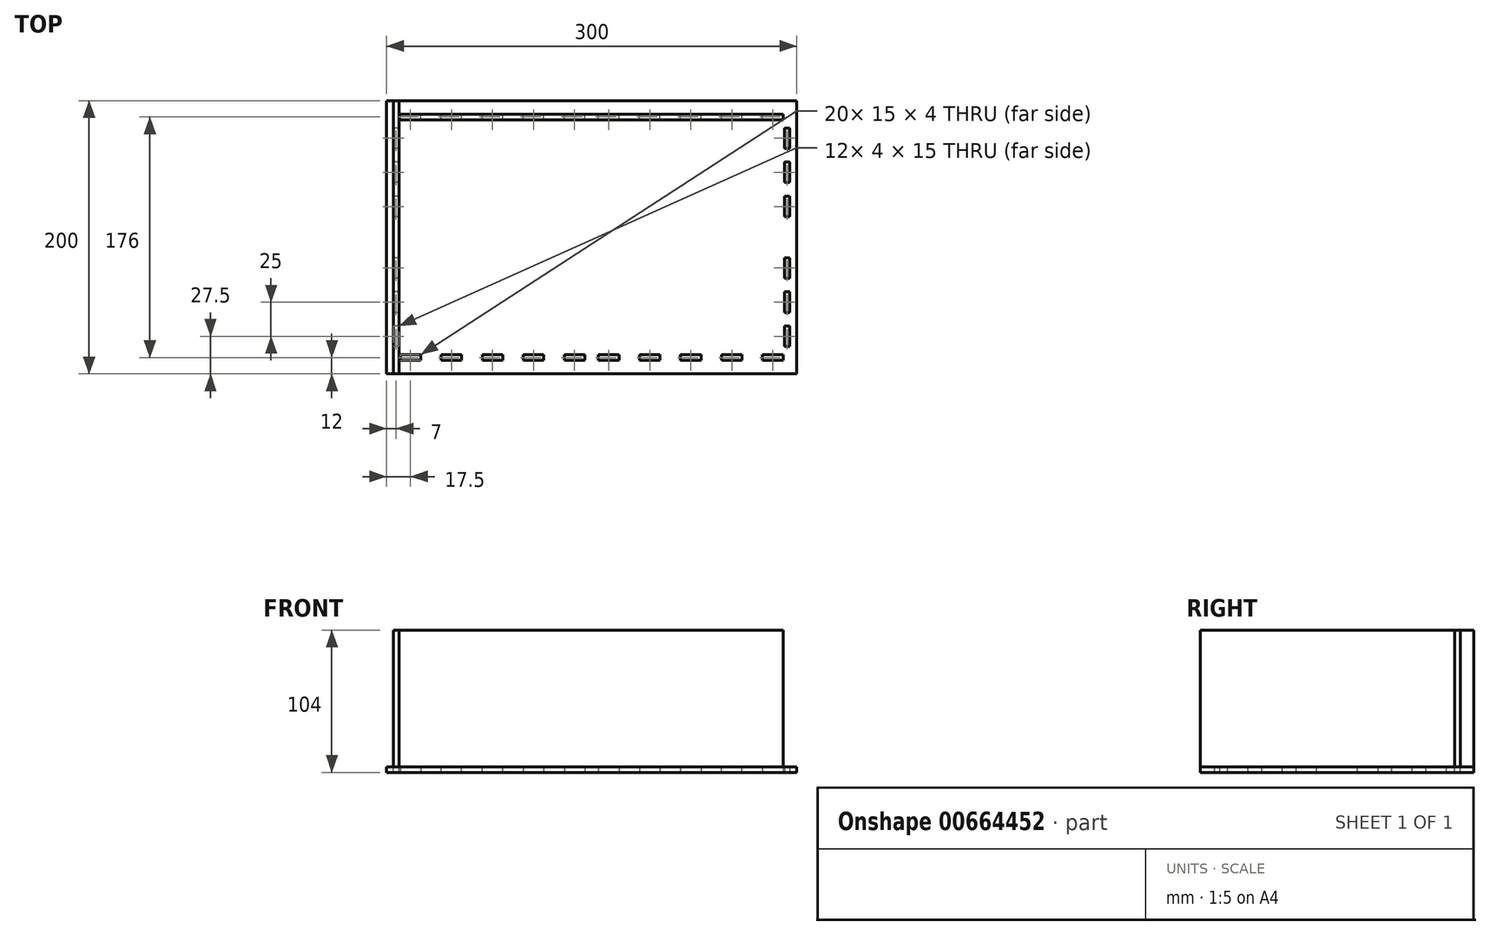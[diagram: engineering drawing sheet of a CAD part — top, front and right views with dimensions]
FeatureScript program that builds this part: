
annotation { "Feature Type Name" : "Feature", "Feature Type Description" : "" }
export const myFeature = defineFeature(function(context is Context, id is Id, definition is map)
    precondition{}
    {
        {
            assignVariable(context, id + "F0", {"name" : "material_thickness", "anyValue" : 4});
        }
        {
            var Q0;
            Q0=qCreatedBy(makeId("Top.planeOp"),FACE);
            var sketch = newSketch(context, id + "F1", { "sketchPlane" : qUnion([Q0])});
            skLineSegment(sketch, "E0.bottom", {"start": v(150, -100) * mm, "end": v(-150, -100) * mm});
            skLineSegment(sketch, "E0.top", {"start": v(150, 100) * mm, "end": v(-150, 100) * mm});
            skLineSegment(sketch, "E0.left", {"start": v(150, -100) * mm, "end": v(150, 100) * mm});
            skLineSegment(sketch, "E0.right", {"start": v(-150, -100) * mm, "end": v(-150, 100) * mm});
            skPoint(sketch, "E0.middle", {"position": v(0, 0) * mm});
            skLineSegment(sketch, "E1", {"start": v(0, 176.5) * mm, "end": v(0, -168.45) * mm, "construction": true});
            skPoint(sketch, "E1.endSnap0", {"position": v(0, -100) * mm});
            skLineSegment(sketch, "E2", {"start": v(-207.53, 0) * mm, "end": v(211.83, 0) * mm, "construction": true});
            skPoint(sketch, "E2.endSnap0", {"position": v(150, 0) * mm});
            skLineSegment(sketch, "E3.bottom", {"start": v(-125, 86) * mm, "end": v(-140, 86) * mm});
            skLineSegment(sketch, "E3.top", {"start": v(-125, 90) * mm, "end": v(-140, 90) * mm});
            skLineSegment(sketch, "E3.left", {"start": v(-125, 86) * mm, "end": v(-125, 90) * mm});
            skLineSegment(sketch, "E3.right", {"start": v(-140, 86) * mm, "end": v(-140, 90) * mm});
            skLineSegment(sketch, "E4.1.0.0", {"start": v(-95, 90) * mm, "end": v(-110, 90) * mm});
            skLineSegment(sketch, "E4.1.0.1", {"start": v(-110, 86) * mm, "end": v(-110, 90) * mm});
            skLineSegment(sketch, "E4.1.0.2", {"start": v(-95, 86) * mm, "end": v(-110, 86) * mm});
            skLineSegment(sketch, "E4.1.0.3", {"start": v(-95, 86) * mm, "end": v(-95, 90) * mm});
            skLineSegment(sketch, "E4.2.0.0", {"start": v(-65, 90) * mm, "end": v(-80, 90) * mm});
            skLineSegment(sketch, "E4.2.0.1", {"start": v(-80, 86) * mm, "end": v(-80, 90) * mm});
            skLineSegment(sketch, "E4.2.0.2", {"start": v(-65, 86) * mm, "end": v(-80, 86) * mm});
            skLineSegment(sketch, "E4.2.0.3", {"start": v(-65, 86) * mm, "end": v(-65, 90) * mm});
            skLineSegment(sketch, "E4.3.0.0", {"start": v(-35, 90) * mm, "end": v(-50, 90) * mm});
            skLineSegment(sketch, "E4.3.0.1", {"start": v(-50, 86) * mm, "end": v(-50, 90) * mm});
            skLineSegment(sketch, "E4.3.0.2", {"start": v(-35, 86) * mm, "end": v(-50, 86) * mm});
            skLineSegment(sketch, "E4.3.0.3", {"start": v(-35, 86) * mm, "end": v(-35, 90) * mm});
            skLineSegment(sketch, "E4.4.0.0", {"start": v(-5, 90) * mm, "end": v(-20, 90) * mm});
            skLineSegment(sketch, "E4.4.0.1", {"start": v(-20, 86) * mm, "end": v(-20, 90) * mm});
            skLineSegment(sketch, "E4.4.0.2", {"start": v(-5, 86) * mm, "end": v(-20, 86) * mm});
            skLineSegment(sketch, "E4.4.0.3", {"start": v(-5, 86) * mm, "end": v(-5, 90) * mm});
            skLineSegment(sketch, "E4.direction1", {"start": v(-140, 90) * mm, "end": v(-110, 90) * mm, "construction": true});
            skLineSegment(sketch, "E5.MirrorCS", {"start": v(5, 90) * mm, "end": v(20, 90) * mm});
            skLineSegment(sketch, "E6.MirrorCS", {"start": v(5, 86) * mm, "end": v(20, 86) * mm});
            skLineSegment(sketch, "E7.MirrorCS", {"start": v(5, 86) * mm, "end": v(5, 90) * mm});
            skLineSegment(sketch, "E8.MirrorCS", {"start": v(20, 86) * mm, "end": v(20, 90) * mm});
            skLineSegment(sketch, "E9.MirrorCS", {"start": v(110, 86) * mm, "end": v(110, 90) * mm});
            skLineSegment(sketch, "E10.MirrorCS", {"start": v(125, 86) * mm, "end": v(125, 90) * mm});
            skLineSegment(sketch, "E11.MirrorCS", {"start": v(50, 86) * mm, "end": v(50, 90) * mm});
            skLineSegment(sketch, "E12.MirrorCS", {"start": v(140, 86) * mm, "end": v(140, 90) * mm});
            skLineSegment(sketch, "E13.MirrorCS", {"start": v(95, 86) * mm, "end": v(95, 90) * mm});
            skLineSegment(sketch, "E14.MirrorCS", {"start": v(35, 86) * mm, "end": v(35, 90) * mm});
            skLineSegment(sketch, "E15.MirrorCS", {"start": v(80, 86) * mm, "end": v(80, 90) * mm});
            skLineSegment(sketch, "E16.MirrorCS", {"start": v(65, 86) * mm, "end": v(65, 90) * mm});
            skLineSegment(sketch, "E17.MirrorCS", {"start": v(125, 90) * mm, "end": v(140, 90) * mm});
            skLineSegment(sketch, "E18.MirrorCS", {"start": v(35, 86) * mm, "end": v(50, 86) * mm});
            skLineSegment(sketch, "E19.MirrorCS", {"start": v(95, 90) * mm, "end": v(110, 90) * mm});
            skLineSegment(sketch, "E20.MirrorCS", {"start": v(65, 86) * mm, "end": v(80, 86) * mm});
            skLineSegment(sketch, "E21.MirrorCS", {"start": v(95, 86) * mm, "end": v(110, 86) * mm});
            skLineSegment(sketch, "E22.MirrorCS", {"start": v(140, 90) * mm, "end": v(110, 90) * mm, "construction": true});
            skLineSegment(sketch, "E23.MirrorCS", {"start": v(65, 90) * mm, "end": v(80, 90) * mm});
            skLineSegment(sketch, "E24.MirrorCS", {"start": v(125, 86) * mm, "end": v(140, 86) * mm});
            skLineSegment(sketch, "E25.MirrorCS", {"start": v(35, 90) * mm, "end": v(50, 90) * mm});
            skLineSegment(sketch, "E26.bottom", {"start": v(141, 80) * mm, "end": v(145, 80) * mm});
            skLineSegment(sketch, "E26.top", {"start": v(141, 65) * mm, "end": v(145, 65) * mm});
            skLineSegment(sketch, "E26.left", {"start": v(141, 80) * mm, "end": v(141, 65) * mm});
            skLineSegment(sketch, "E26.right", {"start": v(145, 80) * mm, "end": v(145, 65) * mm});
            skLineSegment(sketch, "E27.0.1.0", {"start": v(145, 55) * mm, "end": v(145, 40) * mm});
            skLineSegment(sketch, "E27.0.1.1", {"start": v(141, 55) * mm, "end": v(145, 55) * mm});
            skLineSegment(sketch, "E27.0.1.2", {"start": v(141, 55) * mm, "end": v(141, 40) * mm});
            skLineSegment(sketch, "E27.0.1.3", {"start": v(141, 40) * mm, "end": v(145, 40) * mm});
            skLineSegment(sketch, "E27.0.2.0", {"start": v(145, 30) * mm, "end": v(145, 15) * mm});
            skLineSegment(sketch, "E27.0.2.1", {"start": v(141, 30) * mm, "end": v(145, 30) * mm});
            skLineSegment(sketch, "E27.0.2.2", {"start": v(141, 30) * mm, "end": v(141, 15) * mm});
            skLineSegment(sketch, "E27.0.2.3", {"start": v(141, 15) * mm, "end": v(145, 15) * mm});
            skLineSegment(sketch, "E27.direction1", {"start": v(145, 65) * mm, "end": v(170, 65) * mm, "construction": true});
            skLineSegment(sketch, "E27.direction2", {"start": v(145, 65) * mm, "end": v(145, 40) * mm, "construction": true});
            skLineSegment(sketch, "E28.MirrorCS", {"start": v(141, -55) * mm, "end": v(141, -40) * mm});
            skLineSegment(sketch, "E29.MirrorCS", {"start": v(141, -40) * mm, "end": v(145, -40) * mm});
            skLineSegment(sketch, "E30.MirrorCS", {"start": v(141, -30) * mm, "end": v(145, -30) * mm});
            skLineSegment(sketch, "E31.MirrorCS", {"start": v(145, -30) * mm, "end": v(145, -15) * mm});
            skLineSegment(sketch, "E32.MirrorCS", {"start": v(141, -30) * mm, "end": v(141, -15) * mm});
            skLineSegment(sketch, "E33.MirrorCS", {"start": v(141, -15) * mm, "end": v(145, -15) * mm});
            skLineSegment(sketch, "E34.MirrorCS", {"start": v(141, -55) * mm, "end": v(145, -55) * mm});
            skLineSegment(sketch, "E35.MirrorCS", {"start": v(141, -65) * mm, "end": v(145, -65) * mm});
            skLineSegment(sketch, "E36.MirrorCS", {"start": v(145, -80) * mm, "end": v(145, -65) * mm});
            skLineSegment(sketch, "E37.MirrorCS", {"start": v(141, -80) * mm, "end": v(141, -65) * mm});
            skLineSegment(sketch, "E38.MirrorCS", {"start": v(141, -80) * mm, "end": v(145, -80) * mm});
            skLineSegment(sketch, "E39.MirrorCS", {"start": v(145, -55) * mm, "end": v(145, -40) * mm});
            skLineSegment(sketch, "E40.MirrorCS", {"start": v(140, -86) * mm, "end": v(140, -90) * mm});
            skLineSegment(sketch, "E41.MirrorCS", {"start": v(125, -86) * mm, "end": v(140, -86) * mm});
            skLineSegment(sketch, "E42.MirrorCS", {"start": v(125, -86) * mm, "end": v(125, -90) * mm});
            skLineSegment(sketch, "E43.MirrorCS", {"start": v(125, -90) * mm, "end": v(140, -90) * mm});
            skLineSegment(sketch, "E44.MirrorCS", {"start": v(110, -86) * mm, "end": v(110, -90) * mm});
            skLineSegment(sketch, "E45.MirrorCS", {"start": v(95, -90) * mm, "end": v(110, -90) * mm});
            skLineSegment(sketch, "E46.MirrorCS", {"start": v(95, -86) * mm, "end": v(95, -90) * mm});
            skLineSegment(sketch, "E47.MirrorCS", {"start": v(95, -86) * mm, "end": v(110, -86) * mm});
            skLineSegment(sketch, "E48.MirrorCS", {"start": v(80, -86) * mm, "end": v(80, -90) * mm});
            skLineSegment(sketch, "E49.MirrorCS", {"start": v(65, -90) * mm, "end": v(80, -90) * mm});
            skLineSegment(sketch, "E50.MirrorCS", {"start": v(65, -86) * mm, "end": v(65, -90) * mm});
            skLineSegment(sketch, "E51.MirrorCS", {"start": v(65, -86) * mm, "end": v(80, -86) * mm});
            skLineSegment(sketch, "E52.MirrorCS", {"start": v(50, -86) * mm, "end": v(50, -90) * mm});
            skLineSegment(sketch, "E53.MirrorCS", {"start": v(35, -90) * mm, "end": v(50, -90) * mm});
            skLineSegment(sketch, "E54.MirrorCS", {"start": v(35, -86) * mm, "end": v(50, -86) * mm});
            skLineSegment(sketch, "E55.MirrorCS", {"start": v(35, -86) * mm, "end": v(35, -90) * mm});
            skLineSegment(sketch, "E56.MirrorCS", {"start": v(20, -86) * mm, "end": v(20, -90) * mm});
            skLineSegment(sketch, "E57.MirrorCS", {"start": v(5, -90) * mm, "end": v(20, -90) * mm});
            skLineSegment(sketch, "E58.MirrorCS", {"start": v(5, -86) * mm, "end": v(20, -86) * mm});
            skLineSegment(sketch, "E59.MirrorCS", {"start": v(5, -86) * mm, "end": v(5, -90) * mm});
            skLineSegment(sketch, "E60.MirrorCS", {"start": v(-5, -86) * mm, "end": v(-5, -90) * mm});
            skLineSegment(sketch, "E61.MirrorCS", {"start": v(-5, -90) * mm, "end": v(-20, -90) * mm});
            skLineSegment(sketch, "E62.MirrorCS", {"start": v(-5, -86) * mm, "end": v(-20, -86) * mm});
            skLineSegment(sketch, "E63.MirrorCS", {"start": v(-20, -86) * mm, "end": v(-20, -90) * mm});
            skLineSegment(sketch, "E64.MirrorCS", {"start": v(-35, -86) * mm, "end": v(-35, -90) * mm});
            skLineSegment(sketch, "E65.MirrorCS", {"start": v(-35, -90) * mm, "end": v(-50, -90) * mm});
            skLineSegment(sketch, "E66.MirrorCS", {"start": v(-35, -86) * mm, "end": v(-50, -86) * mm});
            skLineSegment(sketch, "E67.MirrorCS", {"start": v(-50, -86) * mm, "end": v(-50, -90) * mm});
            skLineSegment(sketch, "E68.MirrorCS", {"start": v(-65, -86) * mm, "end": v(-65, -90) * mm});
            skLineSegment(sketch, "E69.MirrorCS", {"start": v(-65, -90) * mm, "end": v(-80, -90) * mm});
            skLineSegment(sketch, "E70.MirrorCS", {"start": v(-65, -86) * mm, "end": v(-80, -86) * mm});
            skLineSegment(sketch, "E71.MirrorCS", {"start": v(-80, -86) * mm, "end": v(-80, -90) * mm});
            skLineSegment(sketch, "E72.MirrorCS", {"start": v(-95, -86) * mm, "end": v(-95, -90) * mm});
            skLineSegment(sketch, "E73.MirrorCS", {"start": v(-95, -90) * mm, "end": v(-110, -90) * mm});
            skLineSegment(sketch, "E74.MirrorCS", {"start": v(-95, -86) * mm, "end": v(-110, -86) * mm});
            skLineSegment(sketch, "E75.MirrorCS", {"start": v(-110, -86) * mm, "end": v(-110, -90) * mm});
            skLineSegment(sketch, "E76.MirrorCS", {"start": v(-125, -86) * mm, "end": v(-125, -90) * mm});
            skLineSegment(sketch, "E77.MirrorCS", {"start": v(-125, -86) * mm, "end": v(-140, -86) * mm});
            skLineSegment(sketch, "E78.MirrorCS", {"start": v(-140, -86) * mm, "end": v(-140, -90) * mm});
            skLineSegment(sketch, "E79.MirrorCS", {"start": v(-125, -90) * mm, "end": v(-140, -90) * mm});
            skLineSegment(sketch, "E80.MirrorCS", {"start": v(-141, 80) * mm, "end": v(-145, 80) * mm});
            skLineSegment(sketch, "E81.MirrorCS", {"start": v(-141, 80) * mm, "end": v(-141, 65) * mm});
            skLineSegment(sketch, "E82.MirrorCS", {"start": v(-145, 80) * mm, "end": v(-145, 65) * mm});
            skLineSegment(sketch, "E83.MirrorCS", {"start": v(-141, 65) * mm, "end": v(-145, 65) * mm});
            skLineSegment(sketch, "E84.MirrorCS", {"start": v(-141, 55) * mm, "end": v(-141, 40) * mm});
            skLineSegment(sketch, "E85.MirrorCS", {"start": v(-141, 40) * mm, "end": v(-145, 40) * mm});
            skLineSegment(sketch, "E86.MirrorCS", {"start": v(-141, 55) * mm, "end": v(-145, 55) * mm});
            skLineSegment(sketch, "E87.MirrorCS", {"start": v(-145, 55) * mm, "end": v(-145, 40) * mm});
            skLineSegment(sketch, "E88.MirrorCS", {"start": v(-141, 30) * mm, "end": v(-145, 30) * mm});
            skLineSegment(sketch, "E89.MirrorCS", {"start": v(-141, 30) * mm, "end": v(-141, 15) * mm});
            skLineSegment(sketch, "E90.MirrorCS", {"start": v(-145, 30) * mm, "end": v(-145, 15) * mm});
            skLineSegment(sketch, "E91.MirrorCS", {"start": v(-141, 15) * mm, "end": v(-145, 15) * mm});
            skLineSegment(sketch, "E92.MirrorCS", {"start": v(-141, -30) * mm, "end": v(-141, -15) * mm});
            skLineSegment(sketch, "E93.MirrorCS", {"start": v(-145, -30) * mm, "end": v(-145, -15) * mm});
            skLineSegment(sketch, "E94.MirrorCS", {"start": v(-141, -30) * mm, "end": v(-145, -30) * mm});
            skLineSegment(sketch, "E95.MirrorCS", {"start": v(-141, -15) * mm, "end": v(-145, -15) * mm});
            skLineSegment(sketch, "E96.MirrorCS", {"start": v(-145, -55) * mm, "end": v(-145, -40) * mm});
            skLineSegment(sketch, "E97.MirrorCS", {"start": v(-141, -55) * mm, "end": v(-141, -40) * mm});
            skLineSegment(sketch, "E98.MirrorCS", {"start": v(-141, -55) * mm, "end": v(-145, -55) * mm});
            skLineSegment(sketch, "E99.MirrorCS", {"start": v(-141, -40) * mm, "end": v(-145, -40) * mm});
            skLineSegment(sketch, "E100.MirrorCS", {"start": v(-141, -65) * mm, "end": v(-145, -65) * mm});
            skLineSegment(sketch, "E101.MirrorCS", {"start": v(-141, -80) * mm, "end": v(-141, -65) * mm});
            skLineSegment(sketch, "E102.MirrorCS", {"start": v(-145, -80) * mm, "end": v(-145, -65) * mm});
            skLineSegment(sketch, "E103.MirrorCS", {"start": v(-141, -80) * mm, "end": v(-145, -80) * mm});
            skSolve(sketch);
        }
        {
            var Q0;
            Q0=makeQuery(id+"F1.imprint","IMPRINT",FACE,{"disambiguationData":[TD([[makeQuery(id+"F1.imprint","IMPRINT",EDGE,{"derivedFrom":sQuery(id+"F1.wireOp",EDGE,"E0.bottom")}),-1.0]])]});
            extrude(context, id + "F2", {"entities" : qUnion([Q0]), "depth" : (getVariable(context, 'material_thickness')) * mm});
        }
        {
            var Q0;
            Q0=makeQuery(id+"F2.opExtrude","CAP_FACE",FACE,{"disambiguationData":[OSD([sQuery(id+"F1.wireOp",EDGE,"E0.bottom"),sQuery(id+"F1.wireOp",EDGE,"E0.top"),sQuery(id+"F1.wireOp",EDGE,"E0.left"),sQuery(id+"F1.wireOp",EDGE,"E0.right"),sQuery(id+"F1.wireOp",EDGE,"E3.bottom"),sQuery(id+"F1.wireOp",EDGE,"E3.top"),sQuery(id+"F1.wireOp",EDGE,"E3.left"),sQuery(id+"F1.wireOp",EDGE,"E3.right"),sQuery(id+"F1.wireOp",EDGE,"E4.1.0.0"),sQuery(id+"F1.wireOp",EDGE,"E4.1.0.1"),sQuery(id+"F1.wireOp",EDGE,"E4.1.0.2"),sQuery(id+"F1.wireOp",EDGE,"E4.1.0.3"),sQuery(id+"F1.wireOp",EDGE,"E4.2.0.0"),sQuery(id+"F1.wireOp",EDGE,"E4.2.0.1"),sQuery(id+"F1.wireOp",EDGE,"E4.2.0.2"),sQuery(id+"F1.wireOp",EDGE,"E4.2.0.3"),sQuery(id+"F1.wireOp",EDGE,"E4.3.0.0"),sQuery(id+"F1.wireOp",EDGE,"E4.3.0.1"),sQuery(id+"F1.wireOp",EDGE,"E4.3.0.2"),sQuery(id+"F1.wireOp",EDGE,"E4.3.0.3"),sQuery(id+"F1.wireOp",EDGE,"E4.4.0.0"),sQuery(id+"F1.wireOp",EDGE,"E4.4.0.1"),sQuery(id+"F1.wireOp",EDGE,"E4.4.0.2"),sQuery(id+"F1.wireOp",EDGE,"E4.4.0.3"),sQuery(id+"F1.wireOp",EDGE,"E5.MirrorCS"),sQuery(id+"F1.wireOp",EDGE,"E6.MirrorCS"),sQuery(id+"F1.wireOp",EDGE,"E7.MirrorCS"),sQuery(id+"F1.wireOp",EDGE,"E8.MirrorCS"),sQuery(id+"F1.wireOp",EDGE,"E9.MirrorCS"),sQuery(id+"F1.wireOp",EDGE,"E10.MirrorCS"),sQuery(id+"F1.wireOp",EDGE,"E11.MirrorCS"),sQuery(id+"F1.wireOp",EDGE,"E12.MirrorCS"),sQuery(id+"F1.wireOp",EDGE,"E13.MirrorCS"),sQuery(id+"F1.wireOp",EDGE,"E14.MirrorCS"),sQuery(id+"F1.wireOp",EDGE,"E15.MirrorCS"),sQuery(id+"F1.wireOp",EDGE,"E16.MirrorCS"),sQuery(id+"F1.wireOp",EDGE,"E17.MirrorCS"),sQuery(id+"F1.wireOp",EDGE,"E18.MirrorCS"),sQuery(id+"F1.wireOp",EDGE,"E19.MirrorCS"),sQuery(id+"F1.wireOp",EDGE,"E20.MirrorCS"),sQuery(id+"F1.wireOp",EDGE,"E21.MirrorCS"),sQuery(id+"F1.wireOp",EDGE,"E23.MirrorCS"),sQuery(id+"F1.wireOp",EDGE,"E24.MirrorCS"),sQuery(id+"F1.wireOp",EDGE,"E25.MirrorCS"),sQuery(id+"F1.wireOp",EDGE,"E26.bottom"),sQuery(id+"F1.wireOp",EDGE,"E26.top"),sQuery(id+"F1.wireOp",EDGE,"E26.left"),sQuery(id+"F1.wireOp",EDGE,"E26.right"),sQuery(id+"F1.wireOp",EDGE,"E27.0.1.0"),sQuery(id+"F1.wireOp",EDGE,"E27.0.1.1"),sQuery(id+"F1.wireOp",EDGE,"E27.0.1.2"),sQuery(id+"F1.wireOp",EDGE,"E27.0.1.3"),sQuery(id+"F1.wireOp",EDGE,"E27.0.2.0"),sQuery(id+"F1.wireOp",EDGE,"E27.0.2.1"),sQuery(id+"F1.wireOp",EDGE,"E27.0.2.2"),sQuery(id+"F1.wireOp",EDGE,"E27.0.2.3"),sQuery(id+"F1.wireOp",EDGE,"E28.MirrorCS"),sQuery(id+"F1.wireOp",EDGE,"E30.MirrorCS"),sQuery(id+"F1.wireOp",EDGE,"E31.MirrorCS"),sQuery(id+"F1.wireOp",EDGE,"E32.MirrorCS"),sQuery(id+"F1.wireOp",EDGE,"E33.MirrorCS"),sQuery(id+"F1.wireOp",EDGE,"E29.MirrorCS"),sQuery(id+"F1.wireOp",EDGE,"E34.MirrorCS"),sQuery(id+"F1.wireOp",EDGE,"E35.MirrorCS"),sQuery(id+"F1.wireOp",EDGE,"E36.MirrorCS"),sQuery(id+"F1.wireOp",EDGE,"E37.MirrorCS"),sQuery(id+"F1.wireOp",EDGE,"E38.MirrorCS"),sQuery(id+"F1.wireOp",EDGE,"E39.MirrorCS"),sQuery(id+"F1.wireOp",EDGE,"E40.MirrorCS"),sQuery(id+"F1.wireOp",EDGE,"E41.MirrorCS"),sQuery(id+"F1.wireOp",EDGE,"E42.MirrorCS"),sQuery(id+"F1.wireOp",EDGE,"E43.MirrorCS"),sQuery(id+"F1.wireOp",EDGE,"E44.MirrorCS"),sQuery(id+"F1.wireOp",EDGE,"E45.MirrorCS"),sQuery(id+"F1.wireOp",EDGE,"E46.MirrorCS"),sQuery(id+"F1.wireOp",EDGE,"E47.MirrorCS"),sQuery(id+"F1.wireOp",EDGE,"E48.MirrorCS"),sQuery(id+"F1.wireOp",EDGE,"E49.MirrorCS"),sQuery(id+"F1.wireOp",EDGE,"E50.MirrorCS"),sQuery(id+"F1.wireOp",EDGE,"E51.MirrorCS"),sQuery(id+"F1.wireOp",EDGE,"E52.MirrorCS"),sQuery(id+"F1.wireOp",EDGE,"E53.MirrorCS"),sQuery(id+"F1.wireOp",EDGE,"E54.MirrorCS"),sQuery(id+"F1.wireOp",EDGE,"E55.MirrorCS"),sQuery(id+"F1.wireOp",EDGE,"E56.MirrorCS"),sQuery(id+"F1.wireOp",EDGE,"E57.MirrorCS"),sQuery(id+"F1.wireOp",EDGE,"E58.MirrorCS"),sQuery(id+"F1.wireOp",EDGE,"E59.MirrorCS"),sQuery(id+"F1.wireOp",EDGE,"E60.MirrorCS"),sQuery(id+"F1.wireOp",EDGE,"E61.MirrorCS"),sQuery(id+"F1.wireOp",EDGE,"E62.MirrorCS"),sQuery(id+"F1.wireOp",EDGE,"E63.MirrorCS"),sQuery(id+"F1.wireOp",EDGE,"E64.MirrorCS"),sQuery(id+"F1.wireOp",EDGE,"E65.MirrorCS"),sQuery(id+"F1.wireOp",EDGE,"E66.MirrorCS"),sQuery(id+"F1.wireOp",EDGE,"E67.MirrorCS"),sQuery(id+"F1.wireOp",EDGE,"E68.MirrorCS"),sQuery(id+"F1.wireOp",EDGE,"E69.MirrorCS"),sQuery(id+"F1.wireOp",EDGE,"E70.MirrorCS"),sQuery(id+"F1.wireOp",EDGE,"E71.MirrorCS"),sQuery(id+"F1.wireOp",EDGE,"E72.MirrorCS"),sQuery(id+"F1.wireOp",EDGE,"E73.MirrorCS"),sQuery(id+"F1.wireOp",EDGE,"E74.MirrorCS"),sQuery(id+"F1.wireOp",EDGE,"E75.MirrorCS"),sQuery(id+"F1.wireOp",EDGE,"E76.MirrorCS"),sQuery(id+"F1.wireOp",EDGE,"E77.MirrorCS"),sQuery(id+"F1.wireOp",EDGE,"E78.MirrorCS"),sQuery(id+"F1.wireOp",EDGE,"E79.MirrorCS"),sQuery(id+"F1.wireOp",EDGE,"E80.MirrorCS"),sQuery(id+"F1.wireOp",EDGE,"E81.MirrorCS"),sQuery(id+"F1.wireOp",EDGE,"E82.MirrorCS"),sQuery(id+"F1.wireOp",EDGE,"E83.MirrorCS"),sQuery(id+"F1.wireOp",EDGE,"E84.MirrorCS"),sQuery(id+"F1.wireOp",EDGE,"E85.MirrorCS"),sQuery(id+"F1.wireOp",EDGE,"E86.MirrorCS"),sQuery(id+"F1.wireOp",EDGE,"E87.MirrorCS"),sQuery(id+"F1.wireOp",EDGE,"E88.MirrorCS"),sQuery(id+"F1.wireOp",EDGE,"E89.MirrorCS"),sQuery(id+"F1.wireOp",EDGE,"E90.MirrorCS"),sQuery(id+"F1.wireOp",EDGE,"E91.MirrorCS"),sQuery(id+"F1.wireOp",EDGE,"E92.MirrorCS"),sQuery(id+"F1.wireOp",EDGE,"E93.MirrorCS"),sQuery(id+"F1.wireOp",EDGE,"E94.MirrorCS"),sQuery(id+"F1.wireOp",EDGE,"E95.MirrorCS"),sQuery(id+"F1.wireOp",EDGE,"E96.MirrorCS"),sQuery(id+"F1.wireOp",EDGE,"E97.MirrorCS"),sQuery(id+"F1.wireOp",EDGE,"E98.MirrorCS"),sQuery(id+"F1.wireOp",EDGE,"E99.MirrorCS"),sQuery(id+"F1.wireOp",EDGE,"E100.MirrorCS"),sQuery(id+"F1.wireOp",EDGE,"E101.MirrorCS"),sQuery(id+"F1.wireOp",EDGE,"E102.MirrorCS"),sQuery(id+"F1.wireOp",EDGE,"E103.MirrorCS")])],"isStart":false});
            var sketch = newSketch(context, id + "F3", { "sketchPlane" : qUnion([Q0])});
            skLineSegment(sketch, "E104.bottom", {"start": v(-145, -80) * mm, "end": v(-141, -80) * mm});
            skLineSegment(sketch, "E104.top", {"start": v(-145, -65) * mm, "end": v(-141, -65) * mm});
            skLineSegment(sketch, "E104.left", {"start": v(-145, -80) * mm, "end": v(-145, -65) * mm});
            skLineSegment(sketch, "E104.right", {"start": v(-141, -80) * mm, "end": v(-141, -65) * mm});
            skLineSegment(sketch, "E105.bottom", {"start": v(-145, -55) * mm, "end": v(-141, -55) * mm});
            skLineSegment(sketch, "E105.top", {"start": v(-145, -40) * mm, "end": v(-141, -40) * mm});
            skLineSegment(sketch, "E105.left", {"start": v(-145, -55) * mm, "end": v(-145, -40) * mm});
            skLineSegment(sketch, "E105.right", {"start": v(-141, -55) * mm, "end": v(-141, -40) * mm});
            skLineSegment(sketch, "E106.bottom", {"start": v(-145, -30) * mm, "end": v(-141, -30) * mm});
            skLineSegment(sketch, "E106.top", {"start": v(-145, -15) * mm, "end": v(-141, -15) * mm});
            skLineSegment(sketch, "E106.left", {"start": v(-145, -30) * mm, "end": v(-145, -15) * mm});
            skLineSegment(sketch, "E106.right", {"start": v(-141, -30) * mm, "end": v(-141, -15) * mm});
            skLineSegment(sketch, "E107.bottom", {"start": v(-145, 15) * mm, "end": v(-141, 15) * mm});
            skLineSegment(sketch, "E107.top", {"start": v(-145, 30) * mm, "end": v(-141, 30) * mm});
            skLineSegment(sketch, "E107.left", {"start": v(-145, 15) * mm, "end": v(-145, 30) * mm});
            skLineSegment(sketch, "E107.right", {"start": v(-141, 15) * mm, "end": v(-141, 30) * mm});
            skLineSegment(sketch, "E108.bottom", {"start": v(-145, 40) * mm, "end": v(-141, 40) * mm});
            skLineSegment(sketch, "E108.top", {"start": v(-145, 55) * mm, "end": v(-141, 55) * mm});
            skLineSegment(sketch, "E108.left", {"start": v(-145, 40) * mm, "end": v(-145, 55) * mm});
            skLineSegment(sketch, "E108.right", {"start": v(-141, 40) * mm, "end": v(-141, 55) * mm});
            skLineSegment(sketch, "E109.bottom", {"start": v(-145, 65) * mm, "end": v(-141, 65) * mm});
            skLineSegment(sketch, "E109.top", {"start": v(-145, 80) * mm, "end": v(-141, 80) * mm});
            skLineSegment(sketch, "E109.left", {"start": v(-145, 65) * mm, "end": v(-145, 80) * mm});
            skLineSegment(sketch, "E109.right", {"start": v(-141, 65) * mm, "end": v(-141, 80) * mm});
            skSolve(sketch);
        }
        {
            var Q0;
            Q0=makeQuery(id+"F3.imprint","IMPRINT",FACE,{"disambiguationData":[TD([[makeQuery(id+"F3.imprint","IMPRINT",EDGE,{"derivedFrom":sQuery(id+"F3.wireOp",EDGE,"E104.bottom")}),-1.0]])]});
            var Q1;
            Q1=makeQuery(id+"F3.imprint","IMPRINT",FACE,{"disambiguationData":[TD([[makeQuery(id+"F3.imprint","IMPRINT",EDGE,{"derivedFrom":sQuery(id+"F3.wireOp",EDGE,"E105.bottom")}),-1.0]])]});
            var Q2;
            Q2=makeQuery(id+"F3.imprint","IMPRINT",FACE,{"disambiguationData":[TD([[makeQuery(id+"F3.imprint","IMPRINT",EDGE,{"derivedFrom":sQuery(id+"F3.wireOp",EDGE,"E106.bottom")}),-1.0]])]});
            var Q3;
            Q3=makeQuery(id+"F3.imprint","IMPRINT",FACE,{"disambiguationData":[TD([[makeQuery(id+"F3.imprint","IMPRINT",EDGE,{"derivedFrom":sQuery(id+"F3.wireOp",EDGE,"E107.bottom")}),-1.0]])]});
            var Q4;
            Q4=makeQuery(id+"F3.imprint","IMPRINT",FACE,{"disambiguationData":[TD([[makeQuery(id+"F3.imprint","IMPRINT",EDGE,{"derivedFrom":sQuery(id+"F3.wireOp",EDGE,"E108.bottom")}),-1.0]])]});
            var Q5;
            Q5=makeQuery(id+"F3.imprint","IMPRINT",FACE,{"disambiguationData":[TD([[makeQuery(id+"F3.imprint","IMPRINT",EDGE,{"derivedFrom":sQuery(id+"F3.wireOp",EDGE,"E109.bottom")}),-1.0]])]});
            extrude(context, id + "F4", {"entities" : qUnion([Q0, Q1, Q2, Q3, Q4, Q5]), "oppositeDirection" : true, "depth" : 4 * mm});
        }
        {
            var Q0;
            Q0=makeQuery(id+"F2.opExtrude","CAP_FACE",FACE,{"disambiguationData":[OSD([sQuery(id+"F1.wireOp",EDGE,"E0.bottom"),sQuery(id+"F1.wireOp",EDGE,"E0.top"),sQuery(id+"F1.wireOp",EDGE,"E0.left"),sQuery(id+"F1.wireOp",EDGE,"E0.right"),sQuery(id+"F1.wireOp",EDGE,"E3.bottom"),sQuery(id+"F1.wireOp",EDGE,"E3.top"),sQuery(id+"F1.wireOp",EDGE,"E3.left"),sQuery(id+"F1.wireOp",EDGE,"E3.right"),sQuery(id+"F1.wireOp",EDGE,"E4.1.0.0"),sQuery(id+"F1.wireOp",EDGE,"E4.1.0.1"),sQuery(id+"F1.wireOp",EDGE,"E4.1.0.2"),sQuery(id+"F1.wireOp",EDGE,"E4.1.0.3"),sQuery(id+"F1.wireOp",EDGE,"E4.2.0.0"),sQuery(id+"F1.wireOp",EDGE,"E4.2.0.1"),sQuery(id+"F1.wireOp",EDGE,"E4.2.0.2"),sQuery(id+"F1.wireOp",EDGE,"E4.2.0.3"),sQuery(id+"F1.wireOp",EDGE,"E4.3.0.0"),sQuery(id+"F1.wireOp",EDGE,"E4.3.0.1"),sQuery(id+"F1.wireOp",EDGE,"E4.3.0.2"),sQuery(id+"F1.wireOp",EDGE,"E4.3.0.3"),sQuery(id+"F1.wireOp",EDGE,"E4.4.0.0"),sQuery(id+"F1.wireOp",EDGE,"E4.4.0.1"),sQuery(id+"F1.wireOp",EDGE,"E4.4.0.2"),sQuery(id+"F1.wireOp",EDGE,"E4.4.0.3"),sQuery(id+"F1.wireOp",EDGE,"E5.MirrorCS"),sQuery(id+"F1.wireOp",EDGE,"E6.MirrorCS"),sQuery(id+"F1.wireOp",EDGE,"E7.MirrorCS"),sQuery(id+"F1.wireOp",EDGE,"E8.MirrorCS"),sQuery(id+"F1.wireOp",EDGE,"E9.MirrorCS"),sQuery(id+"F1.wireOp",EDGE,"E10.MirrorCS"),sQuery(id+"F1.wireOp",EDGE,"E11.MirrorCS"),sQuery(id+"F1.wireOp",EDGE,"E12.MirrorCS"),sQuery(id+"F1.wireOp",EDGE,"E13.MirrorCS"),sQuery(id+"F1.wireOp",EDGE,"E14.MirrorCS"),sQuery(id+"F1.wireOp",EDGE,"E15.MirrorCS"),sQuery(id+"F1.wireOp",EDGE,"E16.MirrorCS"),sQuery(id+"F1.wireOp",EDGE,"E17.MirrorCS"),sQuery(id+"F1.wireOp",EDGE,"E18.MirrorCS"),sQuery(id+"F1.wireOp",EDGE,"E19.MirrorCS"),sQuery(id+"F1.wireOp",EDGE,"E20.MirrorCS"),sQuery(id+"F1.wireOp",EDGE,"E21.MirrorCS"),sQuery(id+"F1.wireOp",EDGE,"E23.MirrorCS"),sQuery(id+"F1.wireOp",EDGE,"E24.MirrorCS"),sQuery(id+"F1.wireOp",EDGE,"E25.MirrorCS"),sQuery(id+"F1.wireOp",EDGE,"E26.bottom"),sQuery(id+"F1.wireOp",EDGE,"E26.top"),sQuery(id+"F1.wireOp",EDGE,"E26.left"),sQuery(id+"F1.wireOp",EDGE,"E26.right"),sQuery(id+"F1.wireOp",EDGE,"E27.0.1.0"),sQuery(id+"F1.wireOp",EDGE,"E27.0.1.1"),sQuery(id+"F1.wireOp",EDGE,"E27.0.1.2"),sQuery(id+"F1.wireOp",EDGE,"E27.0.1.3"),sQuery(id+"F1.wireOp",EDGE,"E27.0.2.0"),sQuery(id+"F1.wireOp",EDGE,"E27.0.2.1"),sQuery(id+"F1.wireOp",EDGE,"E27.0.2.2"),sQuery(id+"F1.wireOp",EDGE,"E27.0.2.3"),sQuery(id+"F1.wireOp",EDGE,"E28.MirrorCS"),sQuery(id+"F1.wireOp",EDGE,"E30.MirrorCS"),sQuery(id+"F1.wireOp",EDGE,"E31.MirrorCS"),sQuery(id+"F1.wireOp",EDGE,"E32.MirrorCS"),sQuery(id+"F1.wireOp",EDGE,"E33.MirrorCS"),sQuery(id+"F1.wireOp",EDGE,"E29.MirrorCS"),sQuery(id+"F1.wireOp",EDGE,"E34.MirrorCS"),sQuery(id+"F1.wireOp",EDGE,"E35.MirrorCS"),sQuery(id+"F1.wireOp",EDGE,"E36.MirrorCS"),sQuery(id+"F1.wireOp",EDGE,"E37.MirrorCS"),sQuery(id+"F1.wireOp",EDGE,"E38.MirrorCS"),sQuery(id+"F1.wireOp",EDGE,"E39.MirrorCS"),sQuery(id+"F1.wireOp",EDGE,"E40.MirrorCS"),sQuery(id+"F1.wireOp",EDGE,"E41.MirrorCS"),sQuery(id+"F1.wireOp",EDGE,"E42.MirrorCS"),sQuery(id+"F1.wireOp",EDGE,"E43.MirrorCS"),sQuery(id+"F1.wireOp",EDGE,"E44.MirrorCS"),sQuery(id+"F1.wireOp",EDGE,"E45.MirrorCS"),sQuery(id+"F1.wireOp",EDGE,"E46.MirrorCS"),sQuery(id+"F1.wireOp",EDGE,"E47.MirrorCS"),sQuery(id+"F1.wireOp",EDGE,"E48.MirrorCS"),sQuery(id+"F1.wireOp",EDGE,"E49.MirrorCS"),sQuery(id+"F1.wireOp",EDGE,"E50.MirrorCS"),sQuery(id+"F1.wireOp",EDGE,"E51.MirrorCS"),sQuery(id+"F1.wireOp",EDGE,"E52.MirrorCS"),sQuery(id+"F1.wireOp",EDGE,"E53.MirrorCS"),sQuery(id+"F1.wireOp",EDGE,"E54.MirrorCS"),sQuery(id+"F1.wireOp",EDGE,"E55.MirrorCS"),sQuery(id+"F1.wireOp",EDGE,"E56.MirrorCS"),sQuery(id+"F1.wireOp",EDGE,"E57.MirrorCS"),sQuery(id+"F1.wireOp",EDGE,"E58.MirrorCS"),sQuery(id+"F1.wireOp",EDGE,"E59.MirrorCS"),sQuery(id+"F1.wireOp",EDGE,"E60.MirrorCS"),sQuery(id+"F1.wireOp",EDGE,"E61.MirrorCS"),sQuery(id+"F1.wireOp",EDGE,"E62.MirrorCS"),sQuery(id+"F1.wireOp",EDGE,"E63.MirrorCS"),sQuery(id+"F1.wireOp",EDGE,"E64.MirrorCS"),sQuery(id+"F1.wireOp",EDGE,"E65.MirrorCS"),sQuery(id+"F1.wireOp",EDGE,"E66.MirrorCS"),sQuery(id+"F1.wireOp",EDGE,"E67.MirrorCS"),sQuery(id+"F1.wireOp",EDGE,"E68.MirrorCS"),sQuery(id+"F1.wireOp",EDGE,"E69.MirrorCS"),sQuery(id+"F1.wireOp",EDGE,"E70.MirrorCS"),sQuery(id+"F1.wireOp",EDGE,"E71.MirrorCS"),sQuery(id+"F1.wireOp",EDGE,"E72.MirrorCS"),sQuery(id+"F1.wireOp",EDGE,"E73.MirrorCS"),sQuery(id+"F1.wireOp",EDGE,"E74.MirrorCS"),sQuery(id+"F1.wireOp",EDGE,"E75.MirrorCS"),sQuery(id+"F1.wireOp",EDGE,"E76.MirrorCS"),sQuery(id+"F1.wireOp",EDGE,"E77.MirrorCS"),sQuery(id+"F1.wireOp",EDGE,"E78.MirrorCS"),sQuery(id+"F1.wireOp",EDGE,"E79.MirrorCS"),sQuery(id+"F1.wireOp",EDGE,"E80.MirrorCS"),sQuery(id+"F1.wireOp",EDGE,"E81.MirrorCS"),sQuery(id+"F1.wireOp",EDGE,"E82.MirrorCS"),sQuery(id+"F1.wireOp",EDGE,"E83.MirrorCS"),sQuery(id+"F1.wireOp",EDGE,"E84.MirrorCS"),sQuery(id+"F1.wireOp",EDGE,"E85.MirrorCS"),sQuery(id+"F1.wireOp",EDGE,"E86.MirrorCS"),sQuery(id+"F1.wireOp",EDGE,"E87.MirrorCS"),sQuery(id+"F1.wireOp",EDGE,"E88.MirrorCS"),sQuery(id+"F1.wireOp",EDGE,"E89.MirrorCS"),sQuery(id+"F1.wireOp",EDGE,"E90.MirrorCS"),sQuery(id+"F1.wireOp",EDGE,"E91.MirrorCS"),sQuery(id+"F1.wireOp",EDGE,"E92.MirrorCS"),sQuery(id+"F1.wireOp",EDGE,"E93.MirrorCS"),sQuery(id+"F1.wireOp",EDGE,"E94.MirrorCS"),sQuery(id+"F1.wireOp",EDGE,"E95.MirrorCS"),sQuery(id+"F1.wireOp",EDGE,"E96.MirrorCS"),sQuery(id+"F1.wireOp",EDGE,"E97.MirrorCS"),sQuery(id+"F1.wireOp",EDGE,"E98.MirrorCS"),sQuery(id+"F1.wireOp",EDGE,"E99.MirrorCS"),sQuery(id+"F1.wireOp",EDGE,"E100.MirrorCS"),sQuery(id+"F1.wireOp",EDGE,"E101.MirrorCS"),sQuery(id+"F1.wireOp",EDGE,"E102.MirrorCS"),sQuery(id+"F1.wireOp",EDGE,"E103.MirrorCS")])],"isStart":false});
            var sketch = newSketch(context, id + "F5", { "sketchPlane" : qUnion([Q0])});
            skLineSegment(sketch, "E110.left", {"start": v(-145, -100) * mm, "end": v(-145, 100) * mm});
            skLineSegment(sketch, "E110.right", {"start": v(-141, -100) * mm, "end": v(-141, 100) * mm});
            skLineSegment(sketch, "E111", {"start": v(-141, -100) * mm, "end": v(-145, -100) * mm});
            skLineSegment(sketch, "E112", {"start": v(-141, 100) * mm, "end": v(-145, 100) * mm});
            skSolve(sketch);
        }
        {
            var Q0;
            Q0=qSketchRegion(id+"F5",true);
            extrude(context, id + "F6", {"entities" : qUnion([Q0]), "depth" : 100 * mm});
        }
        {
            var Q0;
            Q0=makeQuery(id+"F4.opExtrude","SWEPT_BODY",BODY,{"disambiguationData":[OSD([sQuery(id+"F3.wireOp",EDGE,"E104.bottom"),sQuery(id+"F3.wireOp",EDGE,"E104.top"),sQuery(id+"F3.wireOp",EDGE,"E104.left"),sQuery(id+"F3.wireOp",EDGE,"E104.right")])]});
            var Q1;
            Q1=makeQuery(id+"F4.opExtrude","SWEPT_BODY",BODY,{"disambiguationData":[OSD([sQuery(id+"F3.wireOp",EDGE,"E105.bottom"),sQuery(id+"F3.wireOp",EDGE,"E105.top"),sQuery(id+"F3.wireOp",EDGE,"E105.left"),sQuery(id+"F3.wireOp",EDGE,"E105.right")])]});
            var Q2;
            Q2=makeQuery(id+"F4.opExtrude","SWEPT_BODY",BODY,{"disambiguationData":[OSD([sQuery(id+"F3.wireOp",EDGE,"E106.bottom"),sQuery(id+"F3.wireOp",EDGE,"E106.top"),sQuery(id+"F3.wireOp",EDGE,"E106.left"),sQuery(id+"F3.wireOp",EDGE,"E106.right")])]});
            var Q3;
            Q3=makeQuery(id+"F4.opExtrude","SWEPT_BODY",BODY,{"disambiguationData":[OSD([sQuery(id+"F3.wireOp",EDGE,"E107.bottom"),sQuery(id+"F3.wireOp",EDGE,"E107.top"),sQuery(id+"F3.wireOp",EDGE,"E107.left"),sQuery(id+"F3.wireOp",EDGE,"E107.right")])]});
            var Q4;
            Q4=makeQuery(id+"F4.opExtrude","SWEPT_BODY",BODY,{"disambiguationData":[OSD([sQuery(id+"F3.wireOp",EDGE,"E108.bottom"),sQuery(id+"F3.wireOp",EDGE,"E108.top"),sQuery(id+"F3.wireOp",EDGE,"E108.left"),sQuery(id+"F3.wireOp",EDGE,"E108.right")])]});
            var Q5;
            Q5=makeQuery(id+"F4.opExtrude","SWEPT_BODY",BODY,{"disambiguationData":[OSD([sQuery(id+"F3.wireOp",EDGE,"E109.bottom"),sQuery(id+"F3.wireOp",EDGE,"E109.top"),sQuery(id+"F3.wireOp",EDGE,"E109.left"),sQuery(id+"F3.wireOp",EDGE,"E109.right")])]});
            var Q6;
            Q6=makeQuery(id+"F6.opExtrude","SWEPT_BODY",BODY,{"disambiguationData":[OSD([sQuery(id+"F5.wireOp",EDGE,"E110.bottom"),sQuery(id+"F5.wireOp",EDGE,"E110.top"),sQuery(id+"F5.wireOp",EDGE,"E110.left"),sQuery(id+"F5.wireOp",EDGE,"E110.right")])]});
            booleanBodies(context, id + "F7", {"operationType" : BooleanOperationType.UNION, "tools" : qUnion([Q0, Q1, Q2, Q3, Q4, Q5, Q6])});
        }
        {
            var Q0;
            Q0=makeQuery(id+"F2.opExtrude","CAP_FACE",FACE,{"disambiguationData":[OSD([sQuery(id+"F1.wireOp",EDGE,"E0.bottom"),sQuery(id+"F1.wireOp",EDGE,"E0.top"),sQuery(id+"F1.wireOp",EDGE,"E0.left"),sQuery(id+"F1.wireOp",EDGE,"E0.right"),sQuery(id+"F1.wireOp",EDGE,"E3.bottom"),sQuery(id+"F1.wireOp",EDGE,"E3.top"),sQuery(id+"F1.wireOp",EDGE,"E3.left"),sQuery(id+"F1.wireOp",EDGE,"E3.right"),sQuery(id+"F1.wireOp",EDGE,"E4.1.0.0"),sQuery(id+"F1.wireOp",EDGE,"E4.1.0.1"),sQuery(id+"F1.wireOp",EDGE,"E4.1.0.2"),sQuery(id+"F1.wireOp",EDGE,"E4.1.0.3"),sQuery(id+"F1.wireOp",EDGE,"E4.2.0.0"),sQuery(id+"F1.wireOp",EDGE,"E4.2.0.1"),sQuery(id+"F1.wireOp",EDGE,"E4.2.0.2"),sQuery(id+"F1.wireOp",EDGE,"E4.2.0.3"),sQuery(id+"F1.wireOp",EDGE,"E4.3.0.0"),sQuery(id+"F1.wireOp",EDGE,"E4.3.0.1"),sQuery(id+"F1.wireOp",EDGE,"E4.3.0.2"),sQuery(id+"F1.wireOp",EDGE,"E4.3.0.3"),sQuery(id+"F1.wireOp",EDGE,"E4.4.0.0"),sQuery(id+"F1.wireOp",EDGE,"E4.4.0.1"),sQuery(id+"F1.wireOp",EDGE,"E4.4.0.2"),sQuery(id+"F1.wireOp",EDGE,"E4.4.0.3"),sQuery(id+"F1.wireOp",EDGE,"E5.MirrorCS"),sQuery(id+"F1.wireOp",EDGE,"E6.MirrorCS"),sQuery(id+"F1.wireOp",EDGE,"E7.MirrorCS"),sQuery(id+"F1.wireOp",EDGE,"E8.MirrorCS"),sQuery(id+"F1.wireOp",EDGE,"E9.MirrorCS"),sQuery(id+"F1.wireOp",EDGE,"E10.MirrorCS"),sQuery(id+"F1.wireOp",EDGE,"E11.MirrorCS"),sQuery(id+"F1.wireOp",EDGE,"E12.MirrorCS"),sQuery(id+"F1.wireOp",EDGE,"E13.MirrorCS"),sQuery(id+"F1.wireOp",EDGE,"E14.MirrorCS"),sQuery(id+"F1.wireOp",EDGE,"E15.MirrorCS"),sQuery(id+"F1.wireOp",EDGE,"E16.MirrorCS"),sQuery(id+"F1.wireOp",EDGE,"E17.MirrorCS"),sQuery(id+"F1.wireOp",EDGE,"E18.MirrorCS"),sQuery(id+"F1.wireOp",EDGE,"E19.MirrorCS"),sQuery(id+"F1.wireOp",EDGE,"E20.MirrorCS"),sQuery(id+"F1.wireOp",EDGE,"E21.MirrorCS"),sQuery(id+"F1.wireOp",EDGE,"E23.MirrorCS"),sQuery(id+"F1.wireOp",EDGE,"E24.MirrorCS"),sQuery(id+"F1.wireOp",EDGE,"E25.MirrorCS"),sQuery(id+"F1.wireOp",EDGE,"E26.bottom"),sQuery(id+"F1.wireOp",EDGE,"E26.top"),sQuery(id+"F1.wireOp",EDGE,"E26.left"),sQuery(id+"F1.wireOp",EDGE,"E26.right"),sQuery(id+"F1.wireOp",EDGE,"E27.0.1.0"),sQuery(id+"F1.wireOp",EDGE,"E27.0.1.1"),sQuery(id+"F1.wireOp",EDGE,"E27.0.1.2"),sQuery(id+"F1.wireOp",EDGE,"E27.0.1.3"),sQuery(id+"F1.wireOp",EDGE,"E27.0.2.0"),sQuery(id+"F1.wireOp",EDGE,"E27.0.2.1"),sQuery(id+"F1.wireOp",EDGE,"E27.0.2.2"),sQuery(id+"F1.wireOp",EDGE,"E27.0.2.3"),sQuery(id+"F1.wireOp",EDGE,"E28.MirrorCS"),sQuery(id+"F1.wireOp",EDGE,"E30.MirrorCS"),sQuery(id+"F1.wireOp",EDGE,"E31.MirrorCS"),sQuery(id+"F1.wireOp",EDGE,"E32.MirrorCS"),sQuery(id+"F1.wireOp",EDGE,"E33.MirrorCS"),sQuery(id+"F1.wireOp",EDGE,"E29.MirrorCS"),sQuery(id+"F1.wireOp",EDGE,"E34.MirrorCS"),sQuery(id+"F1.wireOp",EDGE,"E35.MirrorCS"),sQuery(id+"F1.wireOp",EDGE,"E36.MirrorCS"),sQuery(id+"F1.wireOp",EDGE,"E37.MirrorCS"),sQuery(id+"F1.wireOp",EDGE,"E38.MirrorCS"),sQuery(id+"F1.wireOp",EDGE,"E39.MirrorCS"),sQuery(id+"F1.wireOp",EDGE,"E40.MirrorCS"),sQuery(id+"F1.wireOp",EDGE,"E41.MirrorCS"),sQuery(id+"F1.wireOp",EDGE,"E42.MirrorCS"),sQuery(id+"F1.wireOp",EDGE,"E43.MirrorCS"),sQuery(id+"F1.wireOp",EDGE,"E44.MirrorCS"),sQuery(id+"F1.wireOp",EDGE,"E45.MirrorCS"),sQuery(id+"F1.wireOp",EDGE,"E46.MirrorCS"),sQuery(id+"F1.wireOp",EDGE,"E47.MirrorCS"),sQuery(id+"F1.wireOp",EDGE,"E48.MirrorCS"),sQuery(id+"F1.wireOp",EDGE,"E49.MirrorCS"),sQuery(id+"F1.wireOp",EDGE,"E50.MirrorCS"),sQuery(id+"F1.wireOp",EDGE,"E51.MirrorCS"),sQuery(id+"F1.wireOp",EDGE,"E52.MirrorCS"),sQuery(id+"F1.wireOp",EDGE,"E53.MirrorCS"),sQuery(id+"F1.wireOp",EDGE,"E54.MirrorCS"),sQuery(id+"F1.wireOp",EDGE,"E55.MirrorCS"),sQuery(id+"F1.wireOp",EDGE,"E56.MirrorCS"),sQuery(id+"F1.wireOp",EDGE,"E57.MirrorCS"),sQuery(id+"F1.wireOp",EDGE,"E58.MirrorCS"),sQuery(id+"F1.wireOp",EDGE,"E59.MirrorCS"),sQuery(id+"F1.wireOp",EDGE,"E60.MirrorCS"),sQuery(id+"F1.wireOp",EDGE,"E61.MirrorCS"),sQuery(id+"F1.wireOp",EDGE,"E62.MirrorCS"),sQuery(id+"F1.wireOp",EDGE,"E63.MirrorCS"),sQuery(id+"F1.wireOp",EDGE,"E64.MirrorCS"),sQuery(id+"F1.wireOp",EDGE,"E65.MirrorCS"),sQuery(id+"F1.wireOp",EDGE,"E66.MirrorCS"),sQuery(id+"F1.wireOp",EDGE,"E67.MirrorCS"),sQuery(id+"F1.wireOp",EDGE,"E68.MirrorCS"),sQuery(id+"F1.wireOp",EDGE,"E69.MirrorCS"),sQuery(id+"F1.wireOp",EDGE,"E70.MirrorCS"),sQuery(id+"F1.wireOp",EDGE,"E71.MirrorCS"),sQuery(id+"F1.wireOp",EDGE,"E72.MirrorCS"),sQuery(id+"F1.wireOp",EDGE,"E73.MirrorCS"),sQuery(id+"F1.wireOp",EDGE,"E74.MirrorCS"),sQuery(id+"F1.wireOp",EDGE,"E75.MirrorCS"),sQuery(id+"F1.wireOp",EDGE,"E76.MirrorCS"),sQuery(id+"F1.wireOp",EDGE,"E77.MirrorCS"),sQuery(id+"F1.wireOp",EDGE,"E78.MirrorCS"),sQuery(id+"F1.wireOp",EDGE,"E79.MirrorCS"),sQuery(id+"F1.wireOp",EDGE,"E80.MirrorCS"),sQuery(id+"F1.wireOp",EDGE,"E81.MirrorCS"),sQuery(id+"F1.wireOp",EDGE,"E82.MirrorCS"),sQuery(id+"F1.wireOp",EDGE,"E83.MirrorCS"),sQuery(id+"F1.wireOp",EDGE,"E84.MirrorCS"),sQuery(id+"F1.wireOp",EDGE,"E85.MirrorCS"),sQuery(id+"F1.wireOp",EDGE,"E86.MirrorCS"),sQuery(id+"F1.wireOp",EDGE,"E87.MirrorCS"),sQuery(id+"F1.wireOp",EDGE,"E88.MirrorCS"),sQuery(id+"F1.wireOp",EDGE,"E89.MirrorCS"),sQuery(id+"F1.wireOp",EDGE,"E90.MirrorCS"),sQuery(id+"F1.wireOp",EDGE,"E91.MirrorCS"),sQuery(id+"F1.wireOp",EDGE,"E92.MirrorCS"),sQuery(id+"F1.wireOp",EDGE,"E93.MirrorCS"),sQuery(id+"F1.wireOp",EDGE,"E94.MirrorCS"),sQuery(id+"F1.wireOp",EDGE,"E95.MirrorCS"),sQuery(id+"F1.wireOp",EDGE,"E96.MirrorCS"),sQuery(id+"F1.wireOp",EDGE,"E97.MirrorCS"),sQuery(id+"F1.wireOp",EDGE,"E98.MirrorCS"),sQuery(id+"F1.wireOp",EDGE,"E99.MirrorCS"),sQuery(id+"F1.wireOp",EDGE,"E100.MirrorCS"),sQuery(id+"F1.wireOp",EDGE,"E101.MirrorCS"),sQuery(id+"F1.wireOp",EDGE,"E102.MirrorCS"),sQuery(id+"F1.wireOp",EDGE,"E103.MirrorCS")])],"isStart":false});
            var sketch = newSketch(context, id + "F8", { "sketchPlane" : qUnion([Q0])});
            skLineSegment(sketch, "E113.bottom", {"start": v(-140, 90) * mm, "end": v(-125, 90) * mm});
            skLineSegment(sketch, "E113.top", {"start": v(-140, 86) * mm, "end": v(-125, 86) * mm});
            skLineSegment(sketch, "E113.left", {"start": v(-140, 90) * mm, "end": v(-140, 86) * mm});
            skLineSegment(sketch, "E113.right", {"start": v(-125, 90) * mm, "end": v(-125, 86) * mm});
            skLineSegment(sketch, "E114.bottom", {"start": v(-110, 90) * mm, "end": v(-95, 90) * mm});
            skLineSegment(sketch, "E114.top", {"start": v(-110, 86) * mm, "end": v(-95, 86) * mm});
            skLineSegment(sketch, "E114.left", {"start": v(-110, 90) * mm, "end": v(-110, 86) * mm});
            skLineSegment(sketch, "E114.right", {"start": v(-95, 90) * mm, "end": v(-95, 86) * mm});
            skLineSegment(sketch, "E115.bottom", {"start": v(-80, 90) * mm, "end": v(-65, 90) * mm});
            skLineSegment(sketch, "E115.top", {"start": v(-80, 86) * mm, "end": v(-65, 86) * mm});
            skLineSegment(sketch, "E115.left", {"start": v(-80, 90) * mm, "end": v(-80, 86) * mm});
            skLineSegment(sketch, "E115.right", {"start": v(-65, 90) * mm, "end": v(-65, 86) * mm});
            skLineSegment(sketch, "E116.bottom", {"start": v(-50, 90) * mm, "end": v(-35, 90) * mm});
            skLineSegment(sketch, "E116.top", {"start": v(-50, 86) * mm, "end": v(-35, 86) * mm});
            skLineSegment(sketch, "E116.left", {"start": v(-50, 90) * mm, "end": v(-50, 86) * mm});
            skLineSegment(sketch, "E116.right", {"start": v(-35, 90) * mm, "end": v(-35, 86) * mm});
            skLineSegment(sketch, "E117.bottom", {"start": v(-20, 90) * mm, "end": v(-5, 90) * mm});
            skLineSegment(sketch, "E117.top", {"start": v(-20, 86) * mm, "end": v(-5, 86) * mm});
            skLineSegment(sketch, "E117.left", {"start": v(-20, 90) * mm, "end": v(-20, 86) * mm});
            skLineSegment(sketch, "E117.right", {"start": v(-5, 90) * mm, "end": v(-5, 86) * mm});
            skLineSegment(sketch, "E118.bottom", {"start": v(5, 90) * mm, "end": v(20, 90) * mm});
            skLineSegment(sketch, "E118.top", {"start": v(5, 86) * mm, "end": v(20, 86) * mm});
            skLineSegment(sketch, "E118.left", {"start": v(5, 90) * mm, "end": v(5, 86) * mm});
            skLineSegment(sketch, "E118.right", {"start": v(20, 90) * mm, "end": v(20, 86) * mm});
            skLineSegment(sketch, "E119.bottom", {"start": v(35, 90) * mm, "end": v(50, 90) * mm});
            skLineSegment(sketch, "E119.top", {"start": v(35, 86) * mm, "end": v(50, 86) * mm});
            skLineSegment(sketch, "E119.left", {"start": v(35, 90) * mm, "end": v(35, 86) * mm});
            skLineSegment(sketch, "E119.right", {"start": v(50, 90) * mm, "end": v(50, 86) * mm});
            skLineSegment(sketch, "E120.bottom", {"start": v(65, 90) * mm, "end": v(80, 90) * mm});
            skLineSegment(sketch, "E120.top", {"start": v(65, 86) * mm, "end": v(80, 86) * mm});
            skLineSegment(sketch, "E120.left", {"start": v(65, 90) * mm, "end": v(65, 86) * mm});
            skLineSegment(sketch, "E120.right", {"start": v(80, 90) * mm, "end": v(80, 86) * mm});
            skLineSegment(sketch, "E121.bottom", {"start": v(95, 90) * mm, "end": v(110, 90) * mm});
            skLineSegment(sketch, "E121.top", {"start": v(95, 86) * mm, "end": v(110, 86) * mm});
            skLineSegment(sketch, "E121.left", {"start": v(95, 90) * mm, "end": v(95, 86) * mm});
            skLineSegment(sketch, "E121.right", {"start": v(110, 90) * mm, "end": v(110, 86) * mm});
            skLineSegment(sketch, "E122.bottom", {"start": v(125, 90) * mm, "end": v(140, 90) * mm});
            skLineSegment(sketch, "E122.top", {"start": v(125, 86) * mm, "end": v(140, 86) * mm});
            skLineSegment(sketch, "E122.left", {"start": v(125, 90) * mm, "end": v(125, 86) * mm});
            skLineSegment(sketch, "E122.right", {"start": v(140, 90) * mm, "end": v(140, 86) * mm});
            skSolve(sketch);
        }
        {
            var Q0;
            Q0=qSketchRegion(id+"F8",true);
            extrude(context, id + "F9", {"entities" : qUnion([Q0]), "oppositeDirection" : true, "depth" : 4 * mm});
        }
        {
            var Q0;
            Q0=makeQuery(id+"F2.opExtrude","CAP_FACE",FACE,{"disambiguationData":[OSD([sQuery(id+"F1.wireOp",EDGE,"E0.bottom"),sQuery(id+"F1.wireOp",EDGE,"E0.top"),sQuery(id+"F1.wireOp",EDGE,"E0.left"),sQuery(id+"F1.wireOp",EDGE,"E0.right"),sQuery(id+"F1.wireOp",EDGE,"E3.bottom"),sQuery(id+"F1.wireOp",EDGE,"E3.top"),sQuery(id+"F1.wireOp",EDGE,"E3.left"),sQuery(id+"F1.wireOp",EDGE,"E3.right"),sQuery(id+"F1.wireOp",EDGE,"E4.1.0.0"),sQuery(id+"F1.wireOp",EDGE,"E4.1.0.1"),sQuery(id+"F1.wireOp",EDGE,"E4.1.0.2"),sQuery(id+"F1.wireOp",EDGE,"E4.1.0.3"),sQuery(id+"F1.wireOp",EDGE,"E4.2.0.0"),sQuery(id+"F1.wireOp",EDGE,"E4.2.0.1"),sQuery(id+"F1.wireOp",EDGE,"E4.2.0.2"),sQuery(id+"F1.wireOp",EDGE,"E4.2.0.3"),sQuery(id+"F1.wireOp",EDGE,"E4.3.0.0"),sQuery(id+"F1.wireOp",EDGE,"E4.3.0.1"),sQuery(id+"F1.wireOp",EDGE,"E4.3.0.2"),sQuery(id+"F1.wireOp",EDGE,"E4.3.0.3"),sQuery(id+"F1.wireOp",EDGE,"E4.4.0.0"),sQuery(id+"F1.wireOp",EDGE,"E4.4.0.1"),sQuery(id+"F1.wireOp",EDGE,"E4.4.0.2"),sQuery(id+"F1.wireOp",EDGE,"E4.4.0.3"),sQuery(id+"F1.wireOp",EDGE,"E5.MirrorCS"),sQuery(id+"F1.wireOp",EDGE,"E6.MirrorCS"),sQuery(id+"F1.wireOp",EDGE,"E7.MirrorCS"),sQuery(id+"F1.wireOp",EDGE,"E8.MirrorCS"),sQuery(id+"F1.wireOp",EDGE,"E9.MirrorCS"),sQuery(id+"F1.wireOp",EDGE,"E10.MirrorCS"),sQuery(id+"F1.wireOp",EDGE,"E11.MirrorCS"),sQuery(id+"F1.wireOp",EDGE,"E12.MirrorCS"),sQuery(id+"F1.wireOp",EDGE,"E13.MirrorCS"),sQuery(id+"F1.wireOp",EDGE,"E14.MirrorCS"),sQuery(id+"F1.wireOp",EDGE,"E15.MirrorCS"),sQuery(id+"F1.wireOp",EDGE,"E16.MirrorCS"),sQuery(id+"F1.wireOp",EDGE,"E17.MirrorCS"),sQuery(id+"F1.wireOp",EDGE,"E18.MirrorCS"),sQuery(id+"F1.wireOp",EDGE,"E19.MirrorCS"),sQuery(id+"F1.wireOp",EDGE,"E20.MirrorCS"),sQuery(id+"F1.wireOp",EDGE,"E21.MirrorCS"),sQuery(id+"F1.wireOp",EDGE,"E23.MirrorCS"),sQuery(id+"F1.wireOp",EDGE,"E24.MirrorCS"),sQuery(id+"F1.wireOp",EDGE,"E25.MirrorCS"),sQuery(id+"F1.wireOp",EDGE,"E26.bottom"),sQuery(id+"F1.wireOp",EDGE,"E26.top"),sQuery(id+"F1.wireOp",EDGE,"E26.left"),sQuery(id+"F1.wireOp",EDGE,"E26.right"),sQuery(id+"F1.wireOp",EDGE,"E27.0.1.0"),sQuery(id+"F1.wireOp",EDGE,"E27.0.1.1"),sQuery(id+"F1.wireOp",EDGE,"E27.0.1.2"),sQuery(id+"F1.wireOp",EDGE,"E27.0.1.3"),sQuery(id+"F1.wireOp",EDGE,"E27.0.2.0"),sQuery(id+"F1.wireOp",EDGE,"E27.0.2.1"),sQuery(id+"F1.wireOp",EDGE,"E27.0.2.2"),sQuery(id+"F1.wireOp",EDGE,"E27.0.2.3"),sQuery(id+"F1.wireOp",EDGE,"E28.MirrorCS"),sQuery(id+"F1.wireOp",EDGE,"E30.MirrorCS"),sQuery(id+"F1.wireOp",EDGE,"E31.MirrorCS"),sQuery(id+"F1.wireOp",EDGE,"E32.MirrorCS"),sQuery(id+"F1.wireOp",EDGE,"E33.MirrorCS"),sQuery(id+"F1.wireOp",EDGE,"E29.MirrorCS"),sQuery(id+"F1.wireOp",EDGE,"E34.MirrorCS"),sQuery(id+"F1.wireOp",EDGE,"E35.MirrorCS"),sQuery(id+"F1.wireOp",EDGE,"E36.MirrorCS"),sQuery(id+"F1.wireOp",EDGE,"E37.MirrorCS"),sQuery(id+"F1.wireOp",EDGE,"E38.MirrorCS"),sQuery(id+"F1.wireOp",EDGE,"E39.MirrorCS"),sQuery(id+"F1.wireOp",EDGE,"E40.MirrorCS"),sQuery(id+"F1.wireOp",EDGE,"E41.MirrorCS"),sQuery(id+"F1.wireOp",EDGE,"E42.MirrorCS"),sQuery(id+"F1.wireOp",EDGE,"E43.MirrorCS"),sQuery(id+"F1.wireOp",EDGE,"E44.MirrorCS"),sQuery(id+"F1.wireOp",EDGE,"E45.MirrorCS"),sQuery(id+"F1.wireOp",EDGE,"E46.MirrorCS"),sQuery(id+"F1.wireOp",EDGE,"E47.MirrorCS"),sQuery(id+"F1.wireOp",EDGE,"E48.MirrorCS"),sQuery(id+"F1.wireOp",EDGE,"E49.MirrorCS"),sQuery(id+"F1.wireOp",EDGE,"E50.MirrorCS"),sQuery(id+"F1.wireOp",EDGE,"E51.MirrorCS"),sQuery(id+"F1.wireOp",EDGE,"E52.MirrorCS"),sQuery(id+"F1.wireOp",EDGE,"E53.MirrorCS"),sQuery(id+"F1.wireOp",EDGE,"E54.MirrorCS"),sQuery(id+"F1.wireOp",EDGE,"E55.MirrorCS"),sQuery(id+"F1.wireOp",EDGE,"E56.MirrorCS"),sQuery(id+"F1.wireOp",EDGE,"E57.MirrorCS"),sQuery(id+"F1.wireOp",EDGE,"E58.MirrorCS"),sQuery(id+"F1.wireOp",EDGE,"E59.MirrorCS"),sQuery(id+"F1.wireOp",EDGE,"E60.MirrorCS"),sQuery(id+"F1.wireOp",EDGE,"E61.MirrorCS"),sQuery(id+"F1.wireOp",EDGE,"E62.MirrorCS"),sQuery(id+"F1.wireOp",EDGE,"E63.MirrorCS"),sQuery(id+"F1.wireOp",EDGE,"E64.MirrorCS"),sQuery(id+"F1.wireOp",EDGE,"E65.MirrorCS"),sQuery(id+"F1.wireOp",EDGE,"E66.MirrorCS"),sQuery(id+"F1.wireOp",EDGE,"E67.MirrorCS"),sQuery(id+"F1.wireOp",EDGE,"E68.MirrorCS"),sQuery(id+"F1.wireOp",EDGE,"E69.MirrorCS"),sQuery(id+"F1.wireOp",EDGE,"E70.MirrorCS"),sQuery(id+"F1.wireOp",EDGE,"E71.MirrorCS"),sQuery(id+"F1.wireOp",EDGE,"E72.MirrorCS"),sQuery(id+"F1.wireOp",EDGE,"E73.MirrorCS"),sQuery(id+"F1.wireOp",EDGE,"E74.MirrorCS"),sQuery(id+"F1.wireOp",EDGE,"E75.MirrorCS"),sQuery(id+"F1.wireOp",EDGE,"E76.MirrorCS"),sQuery(id+"F1.wireOp",EDGE,"E77.MirrorCS"),sQuery(id+"F1.wireOp",EDGE,"E78.MirrorCS"),sQuery(id+"F1.wireOp",EDGE,"E79.MirrorCS"),sQuery(id+"F1.wireOp",EDGE,"E80.MirrorCS"),sQuery(id+"F1.wireOp",EDGE,"E81.MirrorCS"),sQuery(id+"F1.wireOp",EDGE,"E82.MirrorCS"),sQuery(id+"F1.wireOp",EDGE,"E83.MirrorCS"),sQuery(id+"F1.wireOp",EDGE,"E84.MirrorCS"),sQuery(id+"F1.wireOp",EDGE,"E85.MirrorCS"),sQuery(id+"F1.wireOp",EDGE,"E86.MirrorCS"),sQuery(id+"F1.wireOp",EDGE,"E87.MirrorCS"),sQuery(id+"F1.wireOp",EDGE,"E88.MirrorCS"),sQuery(id+"F1.wireOp",EDGE,"E89.MirrorCS"),sQuery(id+"F1.wireOp",EDGE,"E90.MirrorCS"),sQuery(id+"F1.wireOp",EDGE,"E91.MirrorCS"),sQuery(id+"F1.wireOp",EDGE,"E92.MirrorCS"),sQuery(id+"F1.wireOp",EDGE,"E93.MirrorCS"),sQuery(id+"F1.wireOp",EDGE,"E94.MirrorCS"),sQuery(id+"F1.wireOp",EDGE,"E95.MirrorCS"),sQuery(id+"F1.wireOp",EDGE,"E96.MirrorCS"),sQuery(id+"F1.wireOp",EDGE,"E97.MirrorCS"),sQuery(id+"F1.wireOp",EDGE,"E98.MirrorCS"),sQuery(id+"F1.wireOp",EDGE,"E99.MirrorCS"),sQuery(id+"F1.wireOp",EDGE,"E100.MirrorCS"),sQuery(id+"F1.wireOp",EDGE,"E101.MirrorCS"),sQuery(id+"F1.wireOp",EDGE,"E102.MirrorCS"),sQuery(id+"F1.wireOp",EDGE,"E103.MirrorCS")])],"isStart":false});
            var sketch = newSketch(context, id + "F10", { "sketchPlane" : qUnion([Q0])});
            skLineSegment(sketch, "E123.bottom", {"start": v(-141, 86) * mm, "end": v(140, 86) * mm});
            skLineSegment(sketch, "E123.top", {"start": v(-141, 90) * mm, "end": v(140, 90) * mm});
            skLineSegment(sketch, "E123.left", {"start": v(-141, 86) * mm, "end": v(-141, 90) * mm});
            skLineSegment(sketch, "E123.right", {"start": v(140, 86) * mm, "end": v(140, 100) * mm});
            skSolve(sketch);
        }
        {
            var Q0;
            Q0=qSketchRegion(id+"F10",true);
            extrude(context, id + "F11", {"entities" : qUnion([Q0]), "depth" : 100 * mm});
        }
    });
